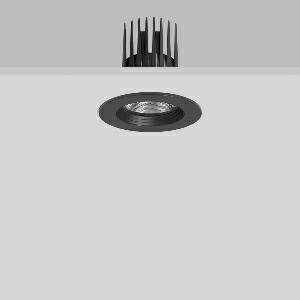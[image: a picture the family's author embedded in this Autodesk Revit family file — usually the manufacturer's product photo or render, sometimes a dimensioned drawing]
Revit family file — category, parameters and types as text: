
# Revit family: heledon_mini_e_901749_003_2_b0e8
name_source: partatom
category: Lighting Fixtures
units: mm (PartAtom-declared; Revit-internal decimal feet)

## family parameters
Cut with Voids When Loaded = No
Host = Face
Light Source = No
Part Type = Normal
Room Calculation Point = No
Round Connector Dimension = Use Diameter
Shared = No

## types (1)
- HELEDON mini E (1 x LED Modul 927, 3300 lm, 2700)
    Apparent Load = 29 VA
    Approval mark = CE
    CIE Flux Codes = 99 100 100 100 100
    Color Rendering = 92
    Color Temperature = 2700
    Default Elevation = 1800 mm
    Description = Series: HELEDON mini
Round recessed downlight. Housing: die-cast aluminium, powder-coated. Black plastic ring and recessed LED to prevent glare from the side. Optical assembly with reflector made of MIRO-Silver with 98% total light reflection for outstanding efficiency - can be changed without tools. Best colour rendering index Ra>90. Suitable for Recessed ceiling mounting. Installation without tools thanks to spring fastening system. Including separate LED converter with connecting cable 600 mm.High quality converter without flickering and stroboscopic effect. Through-wiring box (5 pole) available as accessory. The following accessories can be mounted without use of tools: interchangeable lenses, decorative glasses, honeycomb louvre, clear and frosted diffusers, white interchangeable plastic ring. 
Colour: deep black, matt (RAL 9005)
Diameter: 124 mm
Height: 3 mm
Cut-out diameter: 114 mm
Recess height: 170 mm
Luminaire: recess height: 120 mm
Lamp: LED
Socket: without socket
Colour temperature: 2700K
Colour rendering index (CRI): 92
System power: 29 W
Rated luminous flux: 3300 lm
Luminous efficiency: 114 lm/W
Control gear: Regulated power supply
Protection class: II
Type of protection: IP 20
    Height = 0 mm  [stored 0 ft]
    Lamp = 1 x LED Modul 927
    Lamp Light Flux = 3300 lm
    Lamp count = 1
    Length = 124 mm  [stored 0.406824 ft]
    Lifetime = 50000 h
    Luminous efficacy = 114 lm/W
    Manufacturer = RZB
    ModVariant = No
    Model = 901749.003.2
    Mounting Place = Ceiling
    Mounting Type = Recessed
    Number of Poles = 1
    OnlyDefault = Yes
    Power Factor = 1
    Product Name = HELEDON mini E
    Product group = Recessed downlights
    ProductGroupID = 402
    Protection Class = Protection class II
    Protection Degree = IP 20
    RLX_Detail_Level = 1
    RLX_Emergency_Light_Flux = 0 lm
    RLX_Emergency_Type = 0
    RLX_Emergency_Type_DB = No
    RlxData = <blob elided: 127197 chars, md5=1acdf241>
    Socket = socket
    Standby Power = 0 W
    System Light Flux = 3300 lm
    System Power = 29 W
    Type Comments = Product without accessories
    Type Image = 901657.003.jpg
    URL = http://relux.com
    VarID = ---
    Voltage = 230 V
    Voltage Range = 220-240 V
    Weight = 0.00 kg
    Width = 0 mm  [stored 0 ft]

note: [stored X ft] marks values corroborated as IEEE doubles in the binary element streams (Revit-internal decimal feet)

## geometry (parser evidence)
native form markers: Blend x4, Sweep x11
no freeform markers — native parametric forms only
